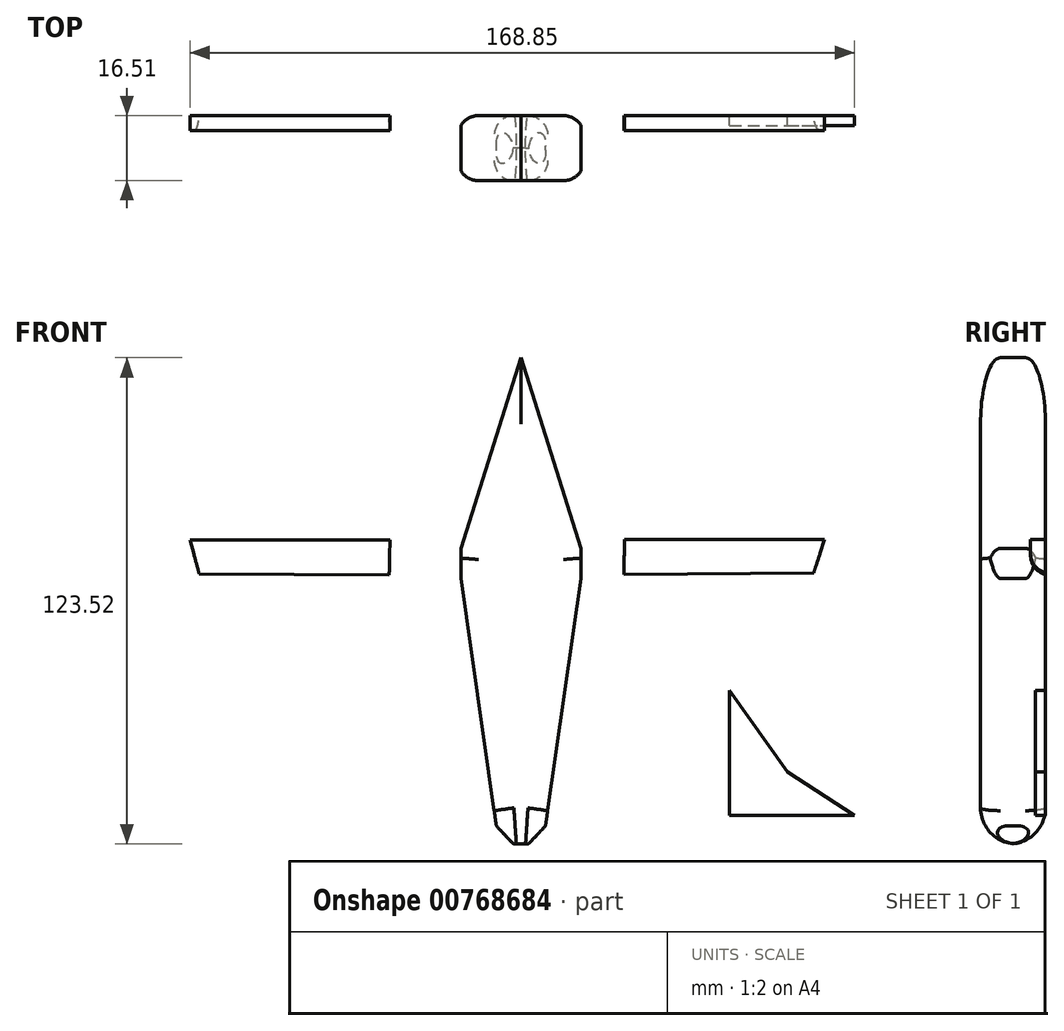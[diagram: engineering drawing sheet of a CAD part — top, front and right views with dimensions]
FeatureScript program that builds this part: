
annotation { "Feature Type Name" : "Feature", "Feature Type Description" : "" }
export const myFeature = defineFeature(function(context is Context, id is Id, definition is map)
    precondition{}
    {
        {
            var Q0;
            Q0=qCreatedBy(makeId("Front.planeOp"),FACE);
            var sketch = newSketch(context, id + "F0", { "sketchPlane" : qUnion([Q0])});
            skLineSegment(sketch, "E0", {"start": v(-49.61, 10.16) * mm, "end": v(-40.6, -52.7) * mm});
            skLineSegment(sketch, "E1", {"start": v(-40.6, -52.7) * mm, "end": v(-36.26, -57.32) * mm});
            skLineSegment(sketch, "E2", {"start": v(-36.26, -57.32) * mm, "end": v(-32.45, -57.32) * mm});
            skLineSegment(sketch, "E3", {"start": v(-32.45, -57.32) * mm, "end": v(-28.1, -52.7) * mm});
            skLineSegment(sketch, "E4", {"start": v(-28.1, -52.7) * mm, "end": v(-19.09, 10.16) * mm});
            skLineSegment(sketch, "E5", {"start": v(-49.61, 17.8) * mm, "end": v(-34.35, 66.24) * mm});
            skLineSegment(sketch, "E6", {"start": v(-19.09, 17.8) * mm, "end": v(-34.35, 66.24) * mm});
            skLineSegment(sketch, "E7", {"start": v(-49.61, 17.8) * mm, "end": v(-49.61, 10.16) * mm});
            skLineSegment(sketch, "E8", {"start": v(-19.09, 17.8) * mm, "end": v(-19.09, 10.16) * mm});
            skSolve(sketch);
        }
        {
            var Q0;
            Q0=qCreatedBy(makeId("Front.planeOp"),FACE);
            var sketch = newSketch(context, id + "F1", { "sketchPlane" : qUnion([Q0])});
            skLineSegment(sketch, "E9", {"start": v(-67.64, 19.88) * mm, "end": v(-118.44, 19.88) * mm});
            skLineSegment(sketch, "E10", {"start": v(-118.44, 19.88) * mm, "end": v(-116.07, 11.3) * mm});
            skLineSegment(sketch, "E11", {"start": v(-116.07, 11.3) * mm, "end": v(-67.81, 10.99) * mm});
            skLineSegment(sketch, "E12", {"start": v(-8.01, 20.05) * mm, "end": v(42.79, 20.05) * mm});
            skLineSegment(sketch, "E13", {"start": v(42.79, 20.05) * mm, "end": v(40.04, 11.6) * mm});
            skLineSegment(sketch, "E14", {"start": v(40.04, 11.6) * mm, "end": v(-8.21, 11.16) * mm});
            skLineSegment(sketch, "E15", {"start": v(-8.01, 20.05) * mm, "end": v(-8.21, 11.16) * mm});
            skLineSegment(sketch, "E16", {"start": v(-67.64, 19.88) * mm, "end": v(-67.81, 10.99) * mm});
            skSolve(sketch);
        }
        {
            var Q0;
            Q0 = qSketchRegion(id + "F1", true);
            extrude(context, id + "F2", {"entities" : qUnion([Q0]), "depth" : 3.8 * mm, "offsetDistance" : 25.4 * mm});
        }
        {
            var Q0;
            Q0 = qSketchRegion(id + "F0", true);
            extrude(context, id + "F3", {"entities" : qUnion([Q0]), "depth" : 16.5 * mm, "offsetDistance" : 25.4 * mm});
        }
        {
            var Q0;
            Q0=qCreatedBy(makeId("Front.planeOp"),FACE);
            var sketch = newSketch(context, id + "F4", { "sketchPlane" : qUnion([Q0])});
            skLineSegment(sketch, "E17", {"start": v(18.66, -18.31) * mm, "end": v(18.66, -50.06) * mm});
            skLineSegment(sketch, "E18", {"start": v(18.66, -50.06) * mm, "end": v(50.41, -50.06) * mm});
            skLineSegment(sketch, "E19", {"start": v(18.66, -18.31) * mm, "end": v(33.34, -39.04) * mm});
            skLineSegment(sketch, "E20", {"start": v(33.34, -39.04) * mm, "end": v(50.41, -50.06) * mm});
            skSolve(sketch);
        }
        {
            var Q0;
            Q0 = qSketchRegion(id + "F4", true);
            extrude(context, id + "F5", {"entities" : qUnion([Q0]), "depth" : 2.54 * mm, "offsetDistance" : 25.4 * mm});
        }
        {
            var Q0;
            Q0=makeQuery(id+"F3.opExtrude","CAP_EDGE",EDGE,{"disambiguationData":[OSD([sQuery(id+"F0.wireOp",EDGE,"E2")])],"isStart":false});
            var Q1;
            Q1=makeQuery(id+"F3.opExtrude","CAP_EDGE",EDGE,{"disambiguationData":[OSD([sQuery(id+"F0.wireOp",EDGE,"E2")])],"isStart":true});
            fillet(context, id + "F6", {"entities" : qUnion([Q0, Q1]), "radius" : 9.2 * mm, "tangentPropagation" : true, "allowEdgeOverflow" : false});
        }
        {
            var Q0;
            Q0=makeQuery(id+"F3.opExtrude","CAP_EDGE",EDGE,{"disambiguationData":[OSD([sQuery(id+"F0.wireOp",EDGE,"E0")])],"isStart":false});
            var Q1;
            Q1=makeQuery(id+"F3.opExtrude","CAP_EDGE",EDGE,{"disambiguationData":[OSD([sQuery(id+"F0.wireOp",EDGE,"E0")])],"isStart":true});
            var Q2;
            Q2=makeQuery(id+"F3.opExtrude","CAP_EDGE",EDGE,{"disambiguationData":[OSD([sQuery(id+"F0.wireOp",EDGE,"E5")])],"isStart":false});
            var Q3;
            Q3=makeQuery(id+"F3.opExtrude","CAP_EDGE",EDGE,{"disambiguationData":[OSD([sQuery(id+"F0.wireOp",EDGE,"E5")])],"isStart":true});
            var Q4;
            Q4=makeQuery(id+"F3.opExtrude","CAP_EDGE",EDGE,{"disambiguationData":[OSD([sQuery(id+"F0.wireOp",EDGE,"E6")])],"isStart":false});
            var Q5;
            Q5=makeQuery(id+"F3.opExtrude","CAP_EDGE",EDGE,{"disambiguationData":[OSD([sQuery(id+"F0.wireOp",EDGE,"E6")])],"isStart":true});
            var Q6;
            Q6=makeQuery(id+"F3.opExtrude","CAP_EDGE",EDGE,{"disambiguationData":[OSD([sQuery(id+"F0.wireOp",EDGE,"E4")])],"isStart":false});
            var Q7;
            Q7=makeQuery(id+"F3.opExtrude","CAP_EDGE",EDGE,{"disambiguationData":[OSD([sQuery(id+"F0.wireOp",EDGE,"E4")])],"isStart":true});
            fillet(context, id + "F7", {"entities" : qUnion([Q0, Q1, Q2, Q3, Q4, Q5, Q6, Q7]), "radius" : 5.08 * mm, "tangentPropagation" : true, "allowEdgeOverflow" : false});
        }
        {
            var Q0;
            Q0=makeQuery(id+"F2.opExtrude","CAP_EDGE",EDGE,{"disambiguationData":[OSD([sQuery(id+"F1.wireOp",EDGE,"E14")])],"isStart":false});
            fillet(context, id + "F8", {"entities" : qUnion([Q0]), "radius" : 5.08 * mm, "tangentPropagation" : true, "allowEdgeOverflow" : false});
        }
        {
            var Q0;
            Q0=makeQuery(id+"F2.opExtrude","CAP_EDGE",EDGE,{"disambiguationData":[OSD([sQuery(id+"F1.wireOp",EDGE,"E11")])],"isStart":false});
            fillet(context, id + "F9", {"entities" : qUnion([Q0]), "radius" : 5.08 * mm, "tangentPropagation" : true, "allowEdgeOverflow" : false});
        }
    });
